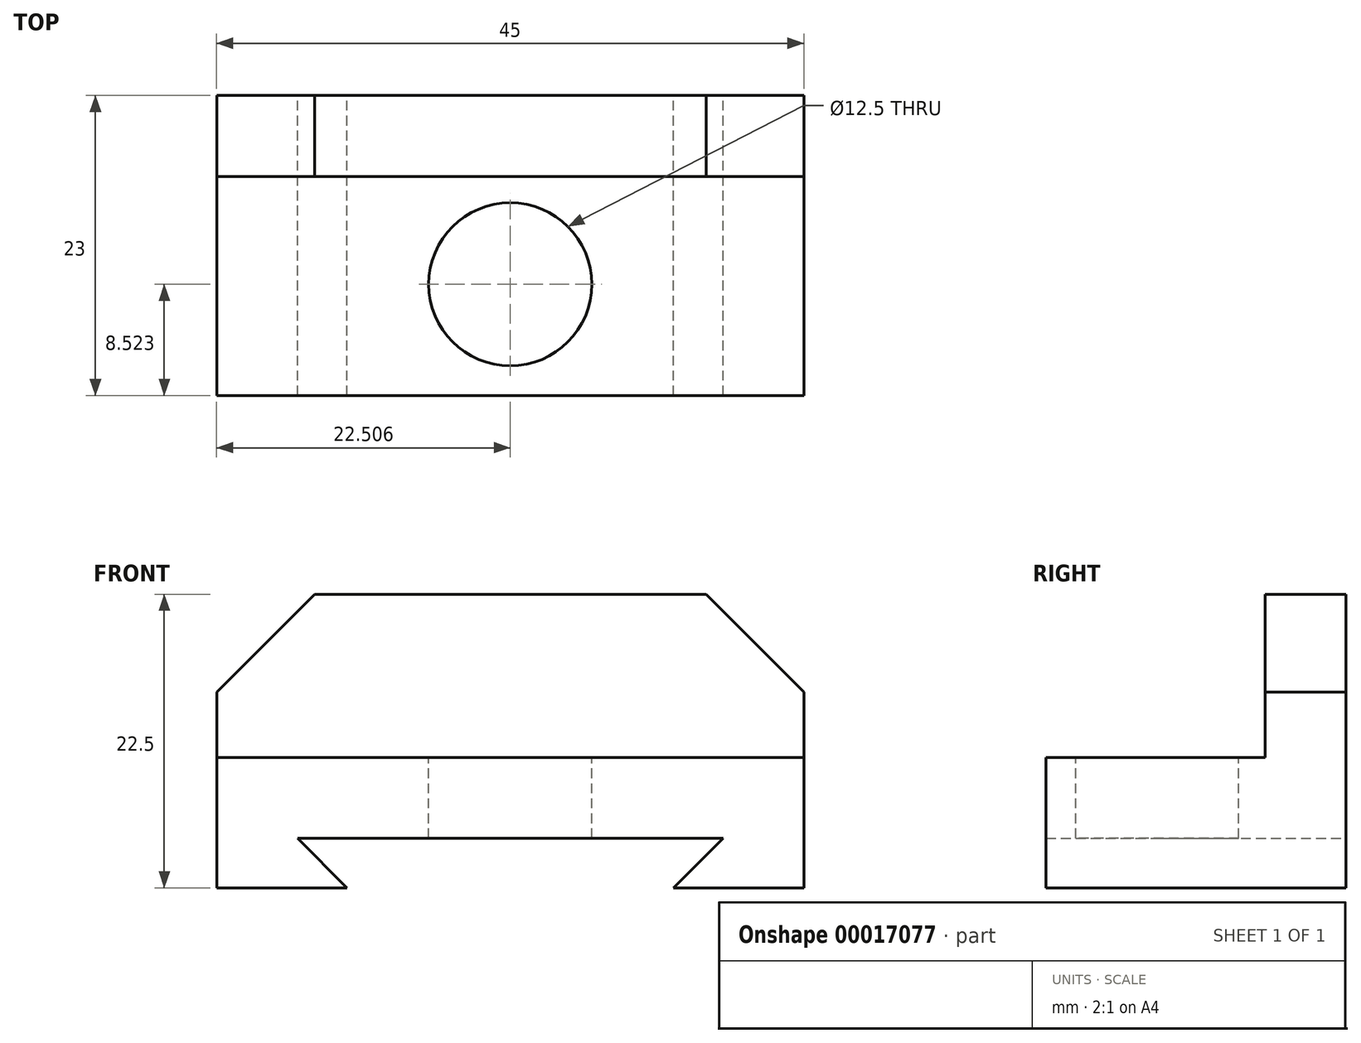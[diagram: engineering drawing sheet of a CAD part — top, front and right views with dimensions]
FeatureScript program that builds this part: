
annotation { "Feature Type Name" : "Feature", "Feature Type Description" : "" }
export const myFeature = defineFeature(function(context is Context, id is Id, definition is map)
    precondition{}
    {
        {
            var Q0;
            Q0=qCreatedBy(makeId("Front.planeOp"),FACE);
            var sketch = newSketch(context, id + "F0", { "sketchPlane" : qUnion([Q0])});
            skLineSegment(sketch, "E0", {"start": v(-18.09, 12.5) * mm, "end": v(-25.59, 5) * mm});
            skLineSegment(sketch, "E1", {"start": v(-25.59, 5) * mm, "end": v(-25.59, 0) * mm});
            skLineSegment(sketch, "E2", {"start": v(-25.59, 0) * mm, "end": v(-25.59, -10) * mm});
            skLineSegment(sketch, "E3", {"start": v(-25.59, -10) * mm, "end": v(-15.59, -10) * mm});
            skLineSegment(sketch, "E4", {"start": v(-15.59, -10) * mm, "end": v(-19.39, -6.2) * mm});
            skLineSegment(sketch, "E5", {"start": v(-19.39, -6.2) * mm, "end": v(13.22, -6.2) * mm});
            skLineSegment(sketch, "E6", {"start": v(13.22, -6.2) * mm, "end": v(9.41, -10) * mm});
            skLineSegment(sketch, "E7", {"start": v(9.41, -10) * mm, "end": v(19.41, -10) * mm});
            skLineSegment(sketch, "E8", {"start": v(19.41, -10) * mm, "end": v(19.41, 0) * mm});
            skLineSegment(sketch, "E9", {"start": v(19.41, 0) * mm, "end": v(19.41, 5) * mm});
            skLineSegment(sketch, "E10", {"start": v(19.41, 5) * mm, "end": v(11.91, 12.5) * mm});
            skLineSegment(sketch, "E11", {"start": v(11.91, 12.5) * mm, "end": v(-18.09, 12.5) * mm});
            skLineSegment(sketch, "E12", {"start": v(-25.59, 0) * mm, "end": v(19.41, 0) * mm});
            skSolve(sketch);
        }
        {
            var Q0;
            Q0=makeQuery(id+"F0.imprint","IMPRINT",FACE,{"disambiguationData":[TD([[makeQuery(id+"F0.imprint","IMPRINT",EDGE,{"derivedFrom":sQuery(id+"F0.wireOp",EDGE,"E2")}),1.0]])]});
            extrude(context, id + "F1", {"entities" : qUnion([Q0]), "depth" : 23 * mm});
        }
        {
            var Q0;
            Q0=makeQuery(id+"F0.imprint","IMPRINT",FACE,{"disambiguationData":[TD([[makeQuery(id+"F0.imprint","IMPRINT",EDGE,{"derivedFrom":sQuery(id+"F0.wireOp",EDGE,"E0")}),1.0]])]});
            extrude(context, id + "F2", {"entities" : qUnion([Q0]), "operationType" : NewBodyOperationType.ADD, "depth" : 6.2 * mm});
        }
        {
            var Q0;
            Q0=makeQuery(id+"F1.opExtrude","SWEPT_FACE",FACE,{"disambiguationData":[OSD([sQuery(id+"F0.wireOp",EDGE,"E12")])]});
            var sketch = newSketch(context, id + "F3", { "sketchPlane" : qUnion([Q0])});
            skLineSegment(sketch, "E13", {"start": v(-25.59, -23) * mm, "end": v(19.41, -6.2) * mm});
            skLineSegment(sketch, "E14", {"start": v(-25.59, -6.2) * mm, "end": v(19.41, -23) * mm});
            skPoint(sketch, "E15", {"position": v(-3.09, -14.6) * mm});
            skCircle(sketch, "E16", {"center": v(-3.08, -14.48) * mm, "radius": 6.25 * mm});
            skSolve(sketch);
        }
        {
            var Q0;
            {var subQ1=sQuery(id+"F3.wireOp",EDGE,"E14");var subQ3=sQuery(id+"F3.wireOp",EDGE,"E13");var subQ5=makeQuery(id+"F3.imprint","INTERSECT",VERTEX,{"derivedFrom":[subQ3,subQ1]});Q0=makeQuery(id+"F3.imprint","IMPRINT",FACE,{"disambiguationData":[TD([[makeQuery(id+"F3.imprint","IMPRINT",EDGE,{"disambiguationData":[TD([[subQ5,-1.0]])],"derivedFrom":subQ3}),1.0]])]});}
            var Q1;
            {var subQ0=sQuery(id+"F3.wireOp",EDGE,"E16");var subQ3=sQuery(id+"F3.wireOp",EDGE,"E13");var subQ4=makeQuery(id+"F3.imprint","INTERSECT",VERTEX,{"disambiguationData":[OD(0.0)],"derivedFrom":[subQ3,subQ0]});Q1=makeQuery(id+"F3.imprint","IMPRINT",FACE,{"disambiguationData":[TD([[makeQuery(id+"F3.imprint","IMPRINT",EDGE,{"disambiguationData":[TD([[subQ4,-1.0]])],"derivedFrom":subQ3}),-1.0]])]});}
            var Q2;
            {var subQ0=sQuery(id+"F3.wireOp",EDGE,"E16");var subQ3=sQuery(id+"F3.wireOp",EDGE,"E13");var subQ4=makeQuery(id+"F3.imprint","INTERSECT",VERTEX,{"disambiguationData":[OD(0.0)],"derivedFrom":[subQ3,subQ0]});Q2=makeQuery(id+"F3.imprint","IMPRINT",FACE,{"disambiguationData":[TD([[makeQuery(id+"F3.imprint","IMPRINT",EDGE,{"disambiguationData":[TD([[subQ4,-1.0]])],"derivedFrom":subQ3}),1.0]])]});}
            var Q3;
            {var subQ1=sQuery(id+"F3.wireOp",EDGE,"E14");var subQ3=sQuery(id+"F3.wireOp",EDGE,"E13");var subQ5=makeQuery(id+"F3.imprint","INTERSECT",VERTEX,{"derivedFrom":[subQ3,subQ1]});Q3=makeQuery(id+"F3.imprint","IMPRINT",FACE,{"disambiguationData":[TD([[makeQuery(id+"F3.imprint","IMPRINT",EDGE,{"disambiguationData":[TD([[subQ5,-1.0]])],"derivedFrom":subQ3}),-1.0]])]});}
            extrude(context, id + "F4", {"entities" : qUnion([Q0, Q1, Q2, Q3]), "operationType" : NewBodyOperationType.REMOVE, "endBound" : BoundingType.THROUGH_ALL, "oppositeDirection" : true, "depth" : 25 * mm});
        }
    });
